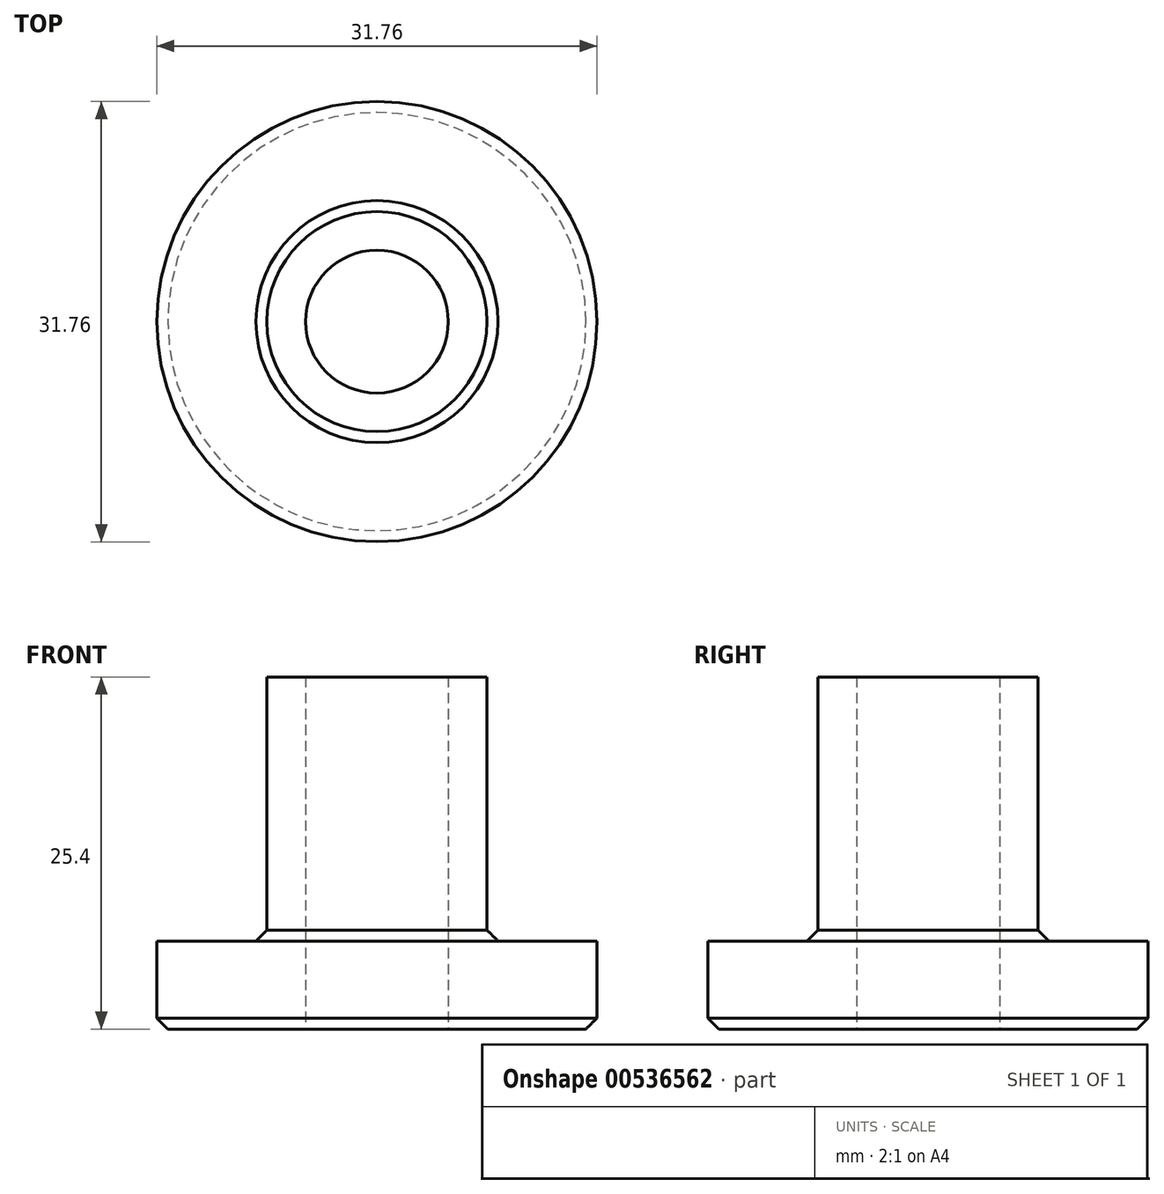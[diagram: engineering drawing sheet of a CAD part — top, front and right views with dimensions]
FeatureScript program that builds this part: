
annotation { "Feature Type Name" : "Feature", "Feature Type Description" : "" }
export const myFeature = defineFeature(function(context is Context, id is Id, definition is map)
    precondition{}
    {
        {
            var Q0;
            Q0=qCreatedBy(makeId("Top.planeOp"),FACE);
            var sketch = newSketch(context, id + "F0", { "sketchPlane" : qUnion([Q0])});
            skCircle(sketch, "E0", {"center": v(0, 0) * mm, "radius": 15.88 * mm});
            skSolve(sketch);
        }
        {
            var Q0;
            Q0 = qSketchRegion(id + "F0", true);
            extrude(context, id + "F1", {"entities" : qUnion([Q0]), "depth" : 25.4 * mm, "offsetDistance" : 25.4 * mm});
        }
        {
            var Q0;
            Q0=sQuery(id+"F0.wireOp",VERTEX,"E0.center");
            var Q1;
            Q1=makeQuery(id+"F1.opExtrude","SWEPT_BODY",BODY,{"disambiguationData":[OSD([sQuery(id+"F0.wireOp",EDGE,"E0")])]});
            hole(context, id + "F2", {"style" : HoleStyle.SIMPLE, "endStyle" : HoleEndStyle.THROUGH, "oppositeDirection" : true, "standardTappedOrClearance" : lookupTablePath({ "standard" : "ISO", "engagement" : "75%", "pitch" : "1.75 mm", "size" : "M12", "type" : "Tapped" }), "standardBlindInLast" : lookupTablePath({ "standard" : "ISO", "engagement" : "75%", "pitch" : "1.75 mm", "size" : "M12", "type" : "Tapped" }), "holeDiameter" : 10.3 * mm, "showTappedDepth" : true, "isTappedThrough" : true, "tappedDepth" : 15.88 * mm, "tapClearance" : 3, "startFromSketch" : true, "locations" : qUnion([Q0]), "scope" : qUnion([Q1]), "majorDiameter" : 12 * mm});
        }
        {
            var Q0;
            Q0=makeQuery(id+"F1.opExtrude","CAP_EDGE",EDGE,{"disambiguationData":[OSD([sQuery(id+"F0.wireOp",EDGE,"E0")])],"isStart":true});
            chamfer(context, id + "F3", {"entities" : qUnion([Q0]), "width" : 0.8 * mm, "tangentPropagation" : true});
        }
        {
            var Q0;
            Q0=makeQuery(id+"F1.opExtrude","CAP_EDGE",EDGE,{"disambiguationData":[OSD([sQuery(id+"F0.wireOp",EDGE,"E0")])],"isStart":false});
            var Q1;
            Q1=makeQuery(id+"F2.hole-0.boolean.opBoolean","COPY",EDGE,{"derivedFrom":makeQuery(id+"F2.hole-0.opRevolve","SWEPT_EDGE",EDGE,{"disambiguationData":[OSD([sQuery(id+"F2.hole-0.sketch.wireOp",EDGE,"core_line_2"),sQuery(id+"F2.hole-0.sketch.wireOp",EDGE,"core_line_3")])]})});
            var Q2;
            Q2=makeQuery(id+"F2.hole-0.boolean.opBoolean","INTERSECT",EDGE,{"derivedFrom":[makeQuery(id+"F1.opExtrude","CAP_FACE",FACE,{"disambiguationData":[OSD([sQuery(id+"F0.wireOp",EDGE,"E0")])],"isStart":false}),makeQuery(id+"F2.hole-0.opRevolve","SWEPT_FACE",FACE,{"disambiguationData":[OSD([sQuery(id+"F2.hole-0.sketch.wireOp",EDGE,"core_line_2")])]})]});
            chamfer(context, id + "F4", {"entities" : qUnion([Q0, Q1, Q2]), "width" : 0.8 * mm, "tangentPropagation" : true});
        }
        {
            var Q0;
            Q0=makeQuery(id+"F1.opExtrude","CAP_FACE",FACE,{"disambiguationData":[OSD([sQuery(id+"F0.wireOp",EDGE,"E0")])],"isStart":false});
            var sketch = newSketch(context, id + "F5", { "sketchPlane" : qUnion([Q0])});
            skCircle(sketch, "E1", {"center": v(0, 0) * mm, "radius": 7.94 * mm});
            skCircle(sketch, "E2", {"center": v(0, 0) * mm, "radius": 15.88 * mm});
            skSolve(sketch);
        }
        {
            var Q0;
            Q0 = qSketchRegion(id + "F5", true);
            extrude(context, id + "F6", {"entities" : qUnion([Q0]), "operationType" : NewBodyOperationType.REMOVE, "oppositeDirection" : true, "depth" : 19.05 * mm, "offsetDistance" : 25.4 * mm});
        }
        {
            var Q0;
            Q0=makeQuery(id+"F6.boolean.opBoolean","COPY",EDGE,{"derivedFrom":makeQuery(id+"F6.opExtrude","CAP_EDGE",EDGE,{"disambiguationData":[OSD([sQuery(id+"F5.wireOp",EDGE,"E2")])],"isStart":false})});
            var Q1;
            Q1=makeQuery(id+"F6.boolean.opBoolean","COPY",EDGE,{"derivedFrom":makeQuery(id+"F6.opExtrude","CAP_EDGE",EDGE,{"disambiguationData":[OSD([sQuery(id+"F5.wireOp",EDGE,"E1")])],"isStart":false})});
            chamfer(context, id + "F7", {"entities" : qUnion([Q0, Q1]), "width" : 0.8 * mm, "tangentPropagation" : true});
        }
    });
